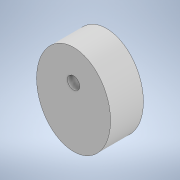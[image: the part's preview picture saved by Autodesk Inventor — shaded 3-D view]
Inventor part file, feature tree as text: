
AUTODESK INVENTOR PART (.ipt)
format: ipt  version: 2021 (Build 250183000, 183)  size: 99,328 bytes
history: native  units: mm
features: extrude x1, sketch x1
ambient origin geometry x8: Origin, YZ Plane, XZ Plane, XY Plane, X Axis, Y Axis, Z Axis, Center Point
bodies: Solid1 (feature_tree)
feature tree (2):
  extrude  "Extrusion1"  Depth=11.0mm
  sketch  "Sketch1"  dims[d0=9.0mm d1=11.0mm d2=3.0mm d3=3.5mm d4=8.0mm d5=0.0mm]
